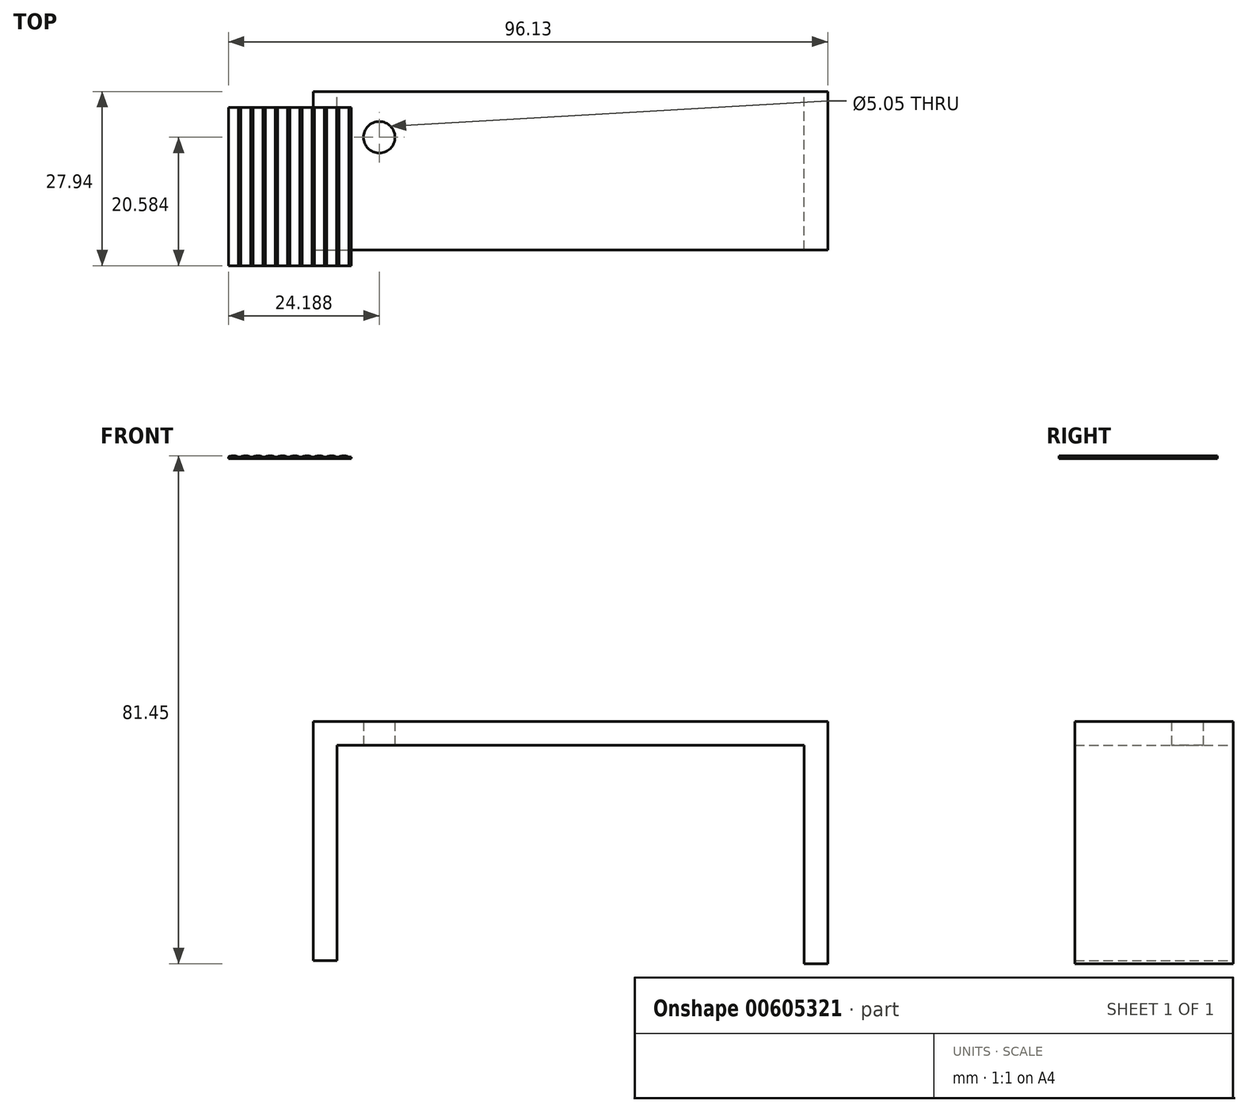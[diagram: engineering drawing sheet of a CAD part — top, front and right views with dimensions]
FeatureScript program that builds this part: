
annotation { "Feature Type Name" : "Feature", "Feature Type Description" : "" }
export const myFeature = defineFeature(function(context is Context, id is Id, definition is map)
    precondition{}
    {
        {
            var Q0;
            Q0=qCreatedBy(makeId("Front.planeOp"),FACE);
            var sketch = newSketch(context, id + "F0", { "sketchPlane" : qUnion([Q0])});
            skLineSegment(sketch, "E0.bottom", {"start": v(-57.31, -44.42) * mm, "end": v(-53.5, -44.42) * mm});
            skLineSegment(sketch, "E0.left", {"start": v(-57.31, -44.42) * mm, "end": v(-57.31, -6.04) * mm});
            skLineSegment(sketch, "E0.right", {"start": v(-53.5, -44.42) * mm, "end": v(-53.5, -9.85) * mm});
            skLineSegment(sketch, "E1.bottom", {"start": v(-53.5, -9.85) * mm, "end": v(21.4, -9.85) * mm});
            skLineSegment(sketch, "E1.top", {"start": v(-57.31, -6.04) * mm, "end": v(25.21, -6.04) * mm});
            skLineSegment(sketch, "E2.top", {"start": v(25.21, -44.87) * mm, "end": v(21.4, -44.87) * mm});
            skLineSegment(sketch, "E2.left", {"start": v(25.21, -6.04) * mm, "end": v(25.21, -44.87) * mm});
            skLineSegment(sketch, "E2.right", {"start": v(21.4, -9.85) * mm, "end": v(21.4, -44.87) * mm});
            skSolve(sketch);
        }
        {
            var Q0;
            Q0=makeQuery(id+"F0.imprint","IMPRINT",FACE,{"disambiguationData":[TD([[makeQuery(id+"F0.imprint","IMPRINT",EDGE,{"derivedFrom":sQuery(id+"F0.wireOp",EDGE,"E0.bottom")}),1.0]])]});
            extrude(context, id + "F1", {"entities" : qUnion([Q0]), "depth" : 25.4 * mm, "offsetDistance" : 25.4 * mm});
        }
        {
            var Q0;
            Q0=qCreatedBy(makeId("Top.planeOp"),FACE);
            var sketch = newSketch(context, id + "F2", { "sketchPlane" : qUnion([Q0])});
            skCircle(sketch, "E3", {"center": v(-46.73, -7.36) * mm, "radius": 2.53 * mm});
            skSolve(sketch);
        }
        {
            var Q0;
            Q0=makeQuery(id+"F2.imprint","IMPRINT",FACE,{"disambiguationData":[TD([[makeQuery(id+"F2.imprint","IMPRINT",EDGE,{"derivedFrom":sQuery(id+"F2.wireOp",EDGE,"E3")}),1.0]])]});
            extrude(context, id + "F3", {"entities" : qUnion([Q0]), "operationType" : NewBodyOperationType.REMOVE, "endBound" : BoundingType.SYMMETRIC, "depth" : 127 * mm, "offsetDistance" : 25.4 * mm});
        }
        {
            var Q0;
            Q0=qCreatedBy(makeId("Front.planeOp"),FACE);
            var sketch = newSketch(context, id + "F4", { "sketchPlane" : qUnion([Q0])});
            skArc(sketch, "E4", {"start": v(-69.34, 36.4) * mm, "mid": v(-70.13, 36.58) * mm, "end": v(-70.92, 36.4) * mm});
            skLineSegment(sketch, "E5", {"start": v(-69.34, 36.4) * mm, "end": v(-68.95, 36.4) * mm});
            skArc(sketch, "E6.1.0.0", {"start": v(-67.37, 36.4) * mm, "mid": v(-68.16, 36.58) * mm, "end": v(-68.95, 36.4) * mm});
            skLineSegment(sketch, "E6.1.0.2", {"start": v(-67.37, 36.4) * mm, "end": v(-66.98, 36.4) * mm});
            skArc(sketch, "E6.2.0.0", {"start": v(-65.4, 36.4) * mm, "mid": v(-66.2, 36.58) * mm, "end": v(-66.98, 36.4) * mm});
            skLineSegment(sketch, "E6.2.0.2", {"start": v(-65.4, 36.4) * mm, "end": v(-65.01, 36.4) * mm});
            skArc(sketch, "E6.3.0.0", {"start": v(-63.44, 36.4) * mm, "mid": v(-64.22, 36.58) * mm, "end": v(-65.01, 36.4) * mm});
            skLineSegment(sketch, "E6.3.0.2", {"start": v(-63.44, 36.4) * mm, "end": v(-63.04, 36.4) * mm});
            skArc(sketch, "E6.4.0.0", {"start": v(-61.47, 36.4) * mm, "mid": v(-62.26, 36.58) * mm, "end": v(-63.04, 36.4) * mm});
            skLineSegment(sketch, "E6.4.0.2", {"start": v(-61.47, 36.4) * mm, "end": v(-61.08, 36.4) * mm});
            skArc(sketch, "E6.5.0.0", {"start": v(-59.5, 36.4) * mm, "mid": v(-60.29, 36.58) * mm, "end": v(-61.08, 36.4) * mm});
            skLineSegment(sketch, "E6.5.0.2", {"start": v(-59.5, 36.4) * mm, "end": v(-59.1, 36.4) * mm});
            skArc(sketch, "E6.6.0.0", {"start": v(-57.53, 36.4) * mm, "mid": v(-58.32, 36.58) * mm, "end": v(-59.1, 36.4) * mm});
            skLineSegment(sketch, "E6.6.0.2", {"start": v(-57.53, 36.4) * mm, "end": v(-57.14, 36.4) * mm});
            skArc(sketch, "E6.7.0.0", {"start": v(-55.56, 36.4) * mm, "mid": v(-56.35, 36.58) * mm, "end": v(-57.14, 36.4) * mm});
            skLineSegment(sketch, "E6.7.0.2", {"start": v(-55.56, 36.4) * mm, "end": v(-55.17, 36.4) * mm});
            skArc(sketch, "E6.8.0.0", {"start": v(-53.6, 36.4) * mm, "mid": v(-54.38, 36.58) * mm, "end": v(-55.17, 36.4) * mm});
            skLineSegment(sketch, "E6.8.0.2", {"start": v(-53.6, 36.4) * mm, "end": v(-53.2, 36.4) * mm});
            skArc(sketch, "E6.9.0.0", {"start": v(-51.63, 36.4) * mm, "mid": v(-52.41, 36.58) * mm, "end": v(-53.2, 36.4) * mm});
            skLineSegment(sketch, "E6.9.0.2", {"start": v(-51.63, 36.4) * mm, "end": v(-51.23, 36.4) * mm});
            skLineSegment(sketch, "E7", {"start": v(-70.92, 36.4) * mm, "end": v(-70.92, 36.12) * mm});
            skLineSegment(sketch, "E8", {"start": v(-70.92, 36.12) * mm, "end": v(-51.25, 36.12) * mm});
            skLineSegment(sketch, "E9", {"start": v(-51.25, 36.12) * mm, "end": v(-51.23, 36.4) * mm});
            skSolve(sketch);
        }
        {
            var Q0;
            Q0=makeQuery(id+"F4.imprint","IMPRINT",FACE,{"disambiguationData":[TD([[makeQuery(id+"F4.imprint","IMPRINT",EDGE,{"derivedFrom":sQuery(id+"F4.wireOp",EDGE,"E4")}),1.0]])]});
            extrude(context, id + "F5", {"entities" : qUnion([Q0]), "depth" : 25.4 * mm, "offsetDistance" : 25.4 * mm});
        }
        {
            var Q0;
            Q0=makeQuery(id+"F5.opExtrude","SWEPT_BODY",BODY,{"disambiguationData":[OSD([sQuery(id+"F4.wireOp",EDGE,"E4"),sQuery(id+"F4.wireOp",EDGE,"E5"),sQuery(id+"F4.wireOp",EDGE,"E6.1.0.0"),sQuery(id+"F4.wireOp",EDGE,"E6.1.0.2"),sQuery(id+"F4.wireOp",EDGE,"E6.2.0.0"),sQuery(id+"F4.wireOp",EDGE,"E6.2.0.2"),sQuery(id+"F4.wireOp",EDGE,"E6.3.0.0"),sQuery(id+"F4.wireOp",EDGE,"E6.3.0.2"),sQuery(id+"F4.wireOp",EDGE,"E6.4.0.0"),sQuery(id+"F4.wireOp",EDGE,"E6.4.0.2"),sQuery(id+"F4.wireOp",EDGE,"E6.5.0.0"),sQuery(id+"F4.wireOp",EDGE,"E6.5.0.2"),sQuery(id+"F4.wireOp",EDGE,"E6.6.0.0"),sQuery(id+"F4.wireOp",EDGE,"E6.6.0.2"),sQuery(id+"F4.wireOp",EDGE,"E6.7.0.0"),sQuery(id+"F4.wireOp",EDGE,"E6.7.0.2"),sQuery(id+"F4.wireOp",EDGE,"E6.8.0.0"),sQuery(id+"F4.wireOp",EDGE,"E6.8.0.2"),sQuery(id+"F4.wireOp",EDGE,"E6.9.0.0"),sQuery(id+"F4.wireOp",EDGE,"E6.9.0.2"),sQuery(id+"F4.wireOp",EDGE,"E7"),sQuery(id+"F4.wireOp",EDGE,"E8"),sQuery(id+"F4.wireOp",EDGE,"E9")])]});
            var Q1;
            Q1=qCreatedBy(makeId("Top.planeOp"),FACE);
            transform(context, id + "F6", {"entities" : qUnion([Q0]), "transformType" : TransformType.TRANSLATION_3D, "dx" : 0 * mm, "dy" : -2.54 * mm, "dz" : 0 * mm, "makeCopy" : false});
        }
    });
